# Revit family: BE_77539_de_DE
name_source: partatom
category: Leuchten
units: mm (PartAtom-declared; Revit-internal decimal feet)

## family parameters
Basisbauteil = Fläche
Beim Laden mit Abzugskörper schneiden = Ja
Bemaßung runder Anschluss = Durchmesser verwenden
Gemeinsam genutzt = Nein
Lichtquelle = Nein
Raumberechnungspunkt = Ja
Teiletyp = Normal

## types (6) — shared parameters
AC/DC = AC/DC
Aktualisierung = 2022-05-19T04:00:07
BEGA_Dummy = Nein
BEGA_Intern = Ja
BEGA_Intern_Konstruktion = Ja
BEGA_Intern_an = Ja
BEGA_Intern_aus = Ja
Befestigungsabstand = 67 mm
Befestigungsbohrung = Ø 4,5 mm
Beschreibung = Flächenscheinwerfer
Beschreibung_Sonderanfertigung = Hier können Sie Informationen zur Sonderanfertigung eintragen.
CE_Konformität = ja
ENEC = ja
Energieeffizienzklasse = LED A++ - A
Farbwiedergabeindex = CRI > 90
Frequenz = 0/50-60 Hz
Gewicht = 2.6 kg
Hersteller = BEGA
Lampe = LED 27.3 W
Lastklassifizierung = Beleuchtung
Lebensdauerkriterien = L70B50 @ 25 °C = 200000 h
Logo = BEGA_Logo.png
Material_02 = BEGA_Oberfläche_Silber_matt
Material_03 = BEGA_Oberfläche_Weiss_matt
Material_06 = BEGA_Oberfläche_Edelstahl_gebürstet
Material_09 = BEGA_Glas_klar
Material_15 = BEGA_Leuchtmedium_matt
Material_17 = BEGA_Reflektor
Material_18 = BEGA_Gummi_schwarz
Produktdatenblatt = https://cdn.bega.com
Scheinlast = 0 VA
Schutzart = IP 65
Schutzklasse = I
Sonderanfertigung = Nein
Spannung = 240 V
Typenbild = 77539.png
URL = https://www.bega.com
Umgebungstemperatur = 25 °C
zero-valued in all types: Vorgabe-Ansicht

## per-type parameters (varying)
| type | BEGA_IES1 | BEGA_IES2 | Bestellnummer | Farbtemperatur | LED_Modulbezeichnung | Lampenlichtstrom | Leuchtenlichtstrom | M_A | M_G | M_W | Modell |
| BEGA_77539_Weiß_K4 | Nein | Ja | 77539WK4 | 4000 K | LED-0935/940 | 4575 lm | 3706 lm | Nein | Nein | Ja | 77539WK4 |
| BEGA_77539_Weiß_K3 | Ja | Nein | 77539WK3 | 3000 K | LED-0935/930 | 4325 lm | 3504 lm | Nein | Nein | Ja | 77539WK3 |
| BEGA_77539_Silber_K4 | Nein | Ja | 77539AK4 | 4000 K | LED-0935/940 | 4575 lm | 3706 lm | Ja | Nein | Nein | 77539AK4 |
| BEGA_77539_Grafit_K4 | Nein | Ja | 77539K4 | 4000 K | LED-0935/940 | 4575 lm | 3706 lm | Nein | Ja | Nein | 77539K4 |
| BEGA_77539_Grafit_K3 | Ja | Nein | 77539K3 | 3000 K | LED-0935/930 | 4325 lm | 3504 lm | Nein | Ja | Nein | 77539K3 |
| BEGA_77539_Silber_K3 | Ja | Nein | 77539AK3 | 3000 K | LED-0935/930 | 4325 lm | 3504 lm | Ja | Nein | Nein | 77539AK3 |

## geometry (parser evidence)
native form markers: Blend x2, Sweep x9
no freeform markers — native parametric forms only
